# Revit family: Kohler Toobi 8965IN-9FP-CP Family
name_source: partatom
category: Generic Models
revit_build: Autodesk Revit 2018 (Build: 20170223_1515(x64)
units: mm (PartAtom-declared; Revit-internal decimal feet)

## family parameters
Can host rebar = No
Cut with Voids When Loaded = No
Host = Face
Part Type = Normal
Room Calculation Point = No
Round Connector Dimension = Use Diameter
Shared = No

## types (1)
- Kohler Toobi 8965IN-9FP-CP Family
    Default Elevation = 1219 mm
    Description = Toobi Recessed Bath & Shower Trim
    Disclamer = Although care has been taken to ensure, to the best of our knowledge, that all data and information contained herein is accurate
to the extent that it relates to either matters of fact or accepted practice at the time of issue. MDFC (Pty) Ltd assumes no responsibility for
any errors in, or misinterpretation of, such data and/ or information or any loss or damage arising from, or related to its use.
    Manufacturer = Kohler CO
    Material = Faucets
    Model = 8965IN-9FP-CP
    Plate Height = 166 mm
    Plate Lenght = 113 mm
    Telephone = 011 050 9000
    URL = http://www.africa.kohlercom

## geometry (parser evidence)
native form markers: Sweep x2
no freeform markers — native parametric forms only
